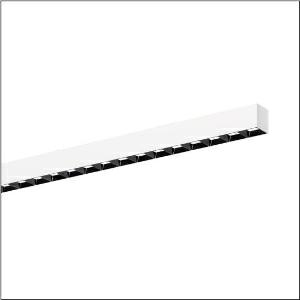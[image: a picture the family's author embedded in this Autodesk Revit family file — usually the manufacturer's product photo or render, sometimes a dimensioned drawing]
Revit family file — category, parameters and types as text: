
# Revit family: silica_r__21_51mx24da44wb_4eb4
name_source: partatom
category: Lighting Fixtures
units: mm (PartAtom-declared; Revit-internal decimal feet)

## family parameters
Cut with Voids When Loaded = No
Host = Face
Light Source = No
Part Type = Normal
Room Calculation Point = No
Round Connector Dimension = Use Diameter
Shared = No

## types (1)
- --- (1 x LED, 4320 lm, 30 W, 4000K)
    Apparent Load = 30 VA
    CIE Flux Codes = 74 94 99 100 100
    Color Rendering = 80
    Color Temperature = 4000K
    Default Elevation = 1800 mm
    Description = Silica® 21, office luminaire, primary light control with darklight reflector, of PMMA, black, CAT 2 (L<= 3000cd/m²), light emission: direct distribution, primary light characteristic: asymmetric, installation type: surface-mounted, LED, rated luminous flux: 4.320lm, luminous efficacy: 144lm/W, light colour: 840, colour temperature: 4000K, with terminal, 3+2-pole, max. 2.5mm², mains connection: 220..240V, AC, 50/60Hz, rated input power: 30W, luminaire housing, of aluminium, traffic white (RAL 9016), length: 1.204mm, width: 53mm, height: 53mm, protection rating (complete): IP20, insulation class (complete): insulation class I (protective earthing), certification: CE, permissible operating ambient temperature: 0..+35°C, standard: EN 50419, packaging unit: 1 piece
    Height = 0 mm  [stored 0 ft]
    Lamp = 1 x LED
    Lamp Light Flux = 4320 lm
    Lamp Power = 30 W
    Lamp count = 1
    Length = 1204 mm
    Luminous efficacy = 144 lm/W
    Manufacturer = Siteco
    ModVariant = No
    Model = 51MX24DA44WB
    Mounting Place = Ceiling
    Mounting Type = Recessed
    Number of Poles = 1
    OnlyDefault = Yes
    Power Factor = 1
    Product Name = Silica® 21
    Product group = office luminaire | ceiling recessed
    ProductGroupID = 401
    Protection Class = Protection class I
    Protection Degree = IP 20
    RLX_Detail_Level = 1
    RLX_Emergency_Light_Flux = 0 lm
    RLX_Emergency_Type = 0
    RLX_Emergency_Type_DB = No
    RlxData = <blob elided: 41521 chars, md5=4aa7780d>
    Socket = socket
    Standby Power = 0 W
    System Light Flux = 4320 lm
    System Power = 30 W
    Type Comments = factory setting: luminous flux: 100 % | dim-lin: 254 | 418 mA
    Type Image = l_1313592.jpg
    URL = http://relux.com
    VarID = @adj_072139
    Voltage = 0 V
    Weight = 0.00 kg
    Width = 53 mm

note: [stored X ft] marks values corroborated as IEEE doubles in the binary element streams (Revit-internal decimal feet)

## geometry (parser evidence)
native form markers: Blend x4, Sweep x9
no freeform markers — native parametric forms only
